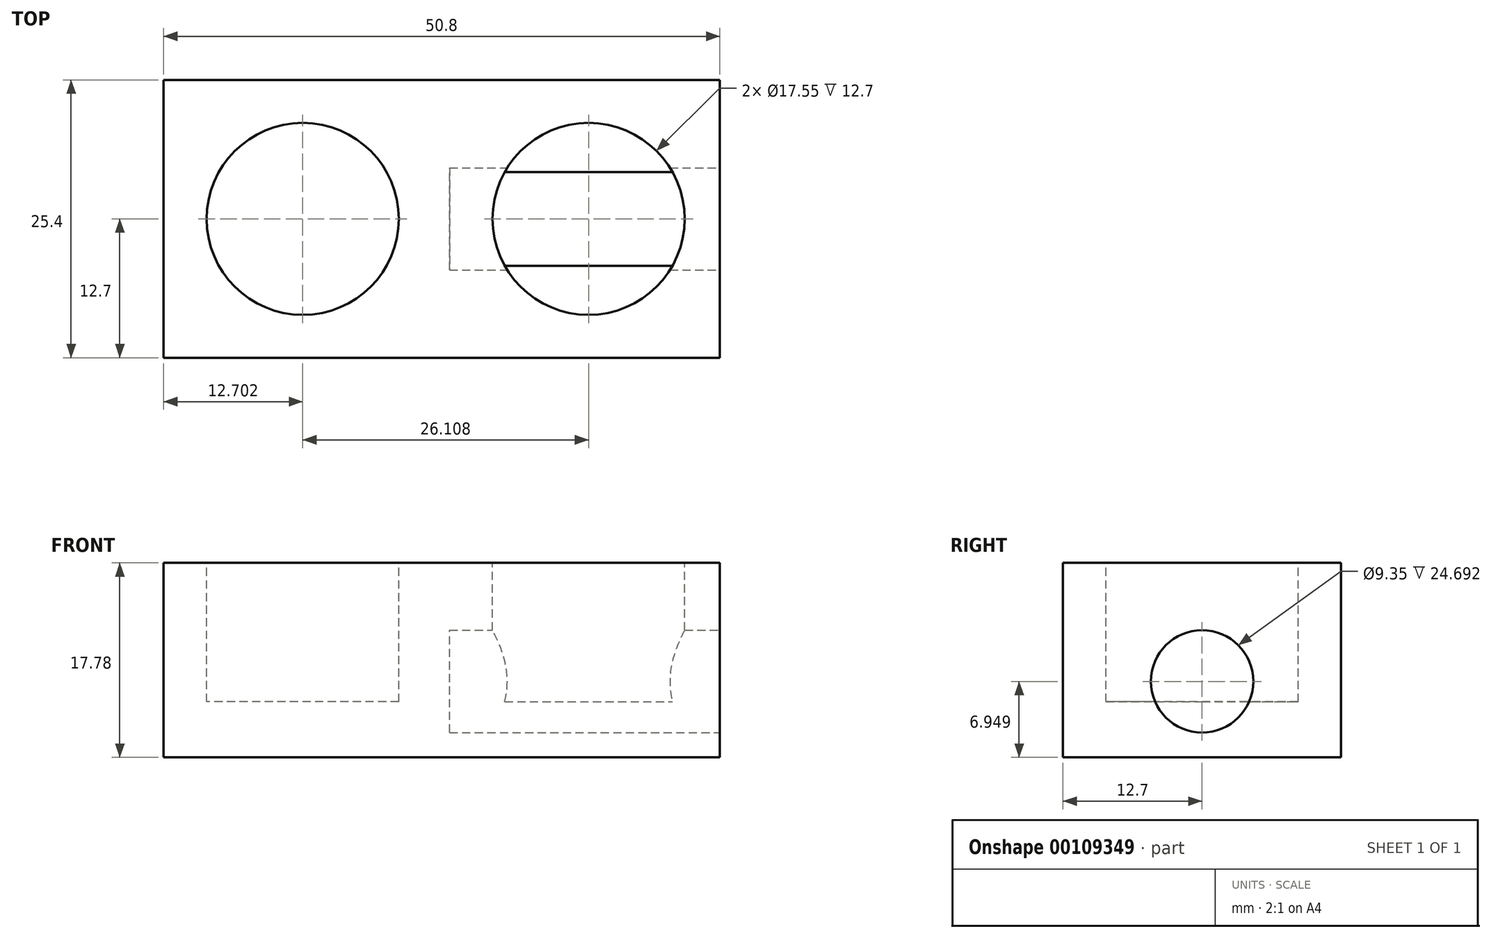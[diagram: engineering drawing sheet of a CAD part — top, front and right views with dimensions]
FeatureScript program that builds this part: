
annotation { "Feature Type Name" : "Feature", "Feature Type Description" : "" }
export const myFeature = defineFeature(function(context is Context, id is Id, definition is map)
    precondition{}
    {
        {
            var Q0;
            Q0=qCreatedBy(makeId("Front.planeOp"),FACE);
            var sketch = newSketch(context, id + "F0", { "sketchPlane" : qUnion([Q0])});
            skLineSegment(sketch, "E0", {"start": v(0, 0) * mm, "end": v(-38.8, 0) * mm});
            skLineSegment(sketch, "E1", {"start": v(0, 0) * mm, "end": v(12, 0) * mm});
            skLineSegment(sketch, "E2", {"start": v(-38.8, 0) * mm, "end": v(-38.8, -17.78) * mm});
            skLineSegment(sketch, "E3", {"start": v(-38.8, -17.78) * mm, "end": v(12, -17.78) * mm});
            skLineSegment(sketch, "E4", {"start": v(12, -17.78) * mm, "end": v(12, 0) * mm});
            skSolve(sketch);
        }
        {
            var Q0;
            Q0 = qSketchRegion(id + "F0", true);
            extrude(context, id + "F1", {"entities" : qUnion([Q0]), "endBound" : BoundingType.SYMMETRIC, "depth" : 25.4 * mm});
        }
        {
            var Q0;
            Q0=qCreatedBy(makeId("Top.planeOp"),FACE);
            var sketch = newSketch(context, id + "F2", { "sketchPlane" : qUnion([Q0])});
            skCircle(sketch, "E5", {"center": v(-26.1, 0) * mm, "radius": 8.78 * mm});
            skCircle(sketch, "E6", {"center": v(0, 0) * mm, "radius": 8.78 * mm});
            skSolve(sketch);
        }
        {
            var Q0;
            Q0 = qSketchRegion(id + "F2", true);
            extrude(context, id + "F3", {"entities" : qUnion([Q0]), "operationType" : NewBodyOperationType.REMOVE, "oppositeDirection" : true, "depth" : 12.7 * mm});
        }
        {
            var Q0;
            Q0=qCreatedBy(makeId("Right.planeOp"),FACE);
            var sketch = newSketch(context, id + "F4", { "sketchPlane" : qUnion([Q0])});
            skCircle(sketch, "E7", {"center": v(0, -10.83) * mm, "radius": 4.67 * mm});
            skSolve(sketch);
        }
        {
            var Q0;
            Q0 = qSketchRegion(id + "F4", true);
            extrude(context, id + "F5", {"entities" : qUnion([Q0]), "operationType" : NewBodyOperationType.REMOVE, "endBound" : BoundingType.SYMMETRIC, "oppositeDirection" : true, "depth" : 25.4 * mm});
        }
    });
